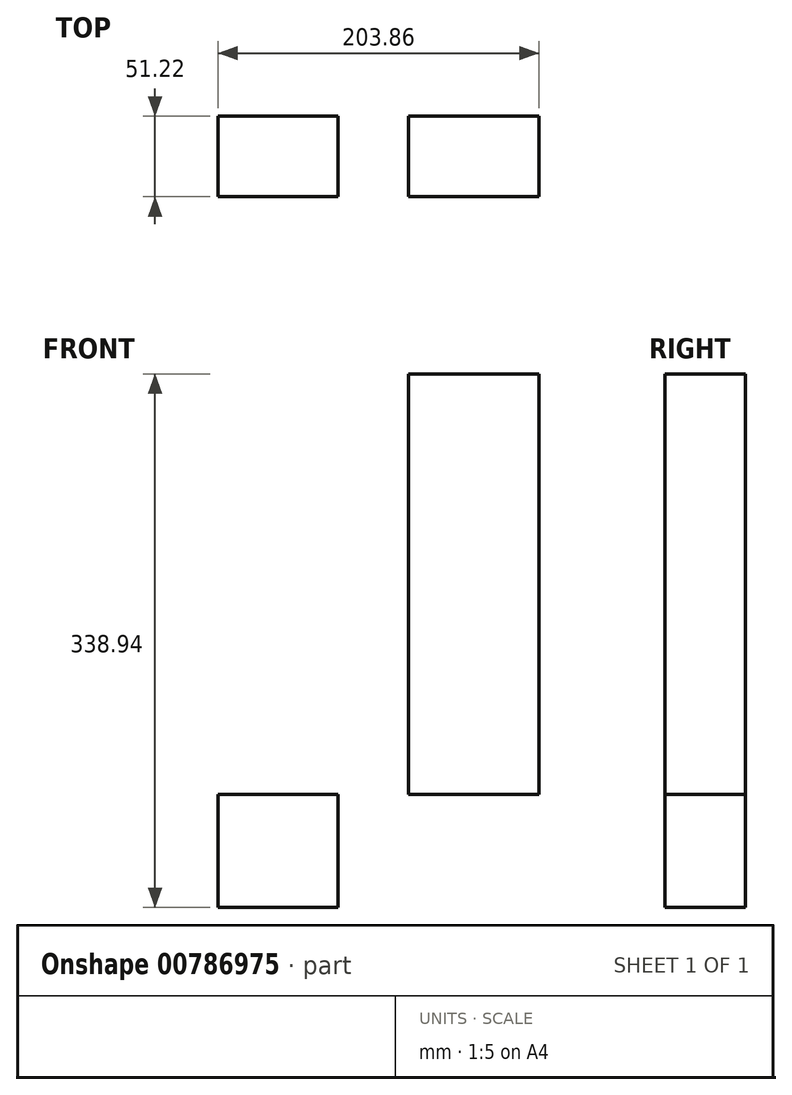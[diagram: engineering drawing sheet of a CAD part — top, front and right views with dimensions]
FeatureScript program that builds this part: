
annotation { "Feature Type Name" : "Feature", "Feature Type Description" : "" }
export const myFeature = defineFeature(function(context is Context, id is Id, definition is map)
    precondition{}
    {
        {
            var Q0;
            Q0=qCreatedBy(makeId("Front.planeOp"),FACE);
            var sketch = newSketch(context, id + "F0", { "sketchPlane" : qUnion([Q0])});
            skLineSegment(sketch, "E0.bottom", {"start": v(0, 16.68) * mm, "end": v(-76.27, 16.68) * mm});
            skLineSegment(sketch, "E0.top", {"start": v(0, -55.12) * mm, "end": v(-76.27, -55.12) * mm});
            skLineSegment(sketch, "E0.left", {"start": v(0, 16.68) * mm, "end": v(0, -55.12) * mm});
            skLineSegment(sketch, "E0.right", {"start": v(-76.27, 16.68) * mm, "end": v(-76.27, -55.12) * mm});
            skPoint(sketch, "E1.oppositeSnap0", {"position": v(-38.14, 16.68) * mm});
            skLineSegment(sketch, "E1.bottom", {"start": v(44.77, 283.82) * mm, "end": v(127.59, 283.82) * mm});
            skLineSegment(sketch, "E1.top", {"start": v(44.77, 16.68) * mm, "end": v(127.59, 16.68) * mm});
            skLineSegment(sketch, "E1.left", {"start": v(44.77, 283.82) * mm, "end": v(44.77, 16.68) * mm});
            skLineSegment(sketch, "E1.right", {"start": v(127.59, 283.82) * mm, "end": v(127.59, 16.68) * mm});
            skSolve(sketch);
        }
        {
            var Q0;
            Q0 = qSketchRegion(id + "F0", true);
            extrude(context, id + "F1", {"entities" : qUnion([Q0]), "depth" : 51.22 * mm, "offsetDistance" : 25.4 * mm});
        }
    });
